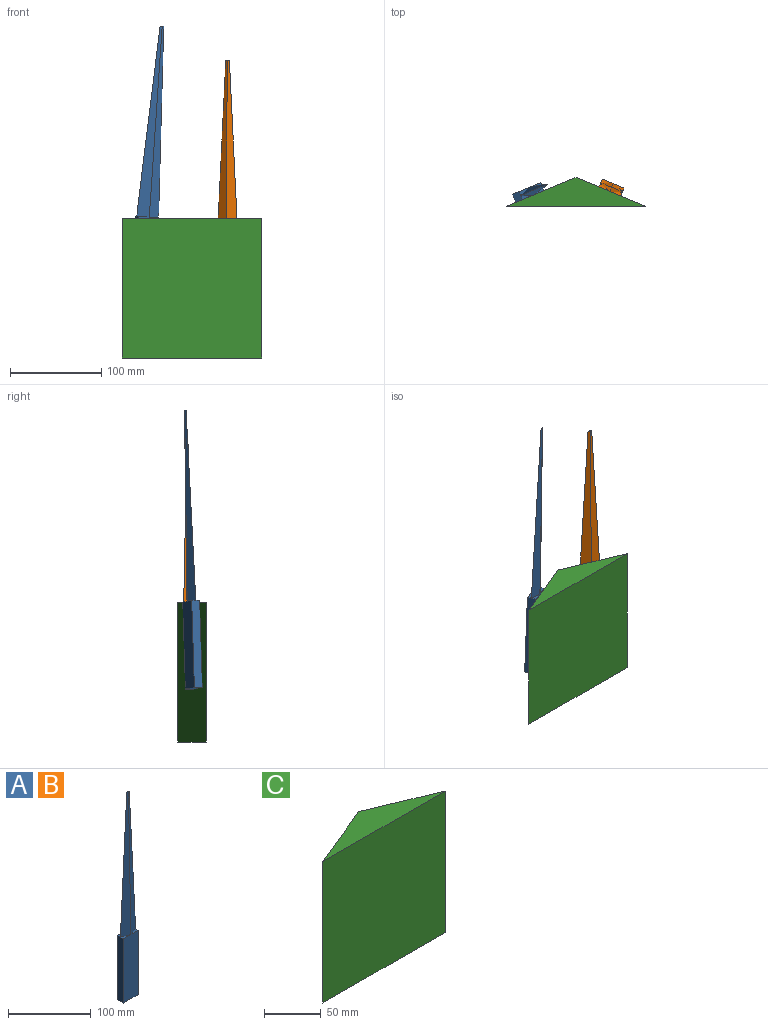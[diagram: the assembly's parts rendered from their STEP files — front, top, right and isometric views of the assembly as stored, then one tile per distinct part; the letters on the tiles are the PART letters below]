
ASSEMBLY  parts=3 mates=2
PART A: 14 faces, bbox 25.4x9.5x304.8 mm
  f0: plane 101.6x9.53mm, normal (1,0,0), area 908.5mm2, adj f1,f3,f5,f6,f7,f10,f11
  f1: plane 101.6x25.4mm, normal (0,1,0), area 2423.7mm2, adj f0,f2,f5,f10,f11,f12,f13
  f2: plane 101.6x9.53mm, normal (-1,0,0), area 908.5mm2, adj f1,f3,f5,f8,f9,f12,f13
  f3: plane 101.6x25.4mm, normal (0,-1,0), area 2423.7mm2, adj f0,f2,f5,f6,f7,f8,f9
  f4: plane 4.27x1.6mm, normal (0,0,1), area 3.4mm2, adj f7,f9,f10,f13
  f5: plane 25.4x9.53mm, normal (0,0,-1), area 241.9mm2, adj f0,f1,f2,f3
  f6: plane 12.37x4.64mm, normal (0,0.02,1), area 28.7mm2, adj f0,f3,f7
  f7: plane 209.55x12.7mm, normal (0.35,-0.94,0.02), area 1694.3mm2, adj f0,f3,f4,f6,f9,f10
  f8: plane 12.37x4.64mm, normal (0,0.02,1), area 28.7mm2, adj f2,f3,f9
  f9: plane 209.55x12.7mm, normal (-0.35,-0.94,0.02), area 1694.3mm2, adj f2,f3,f4,f7,f8,f13
  f10: plane 209.55x12.7mm, normal (0.35,0.94,0.02), area 1694.3mm2, adj f0,f1,f4,f7,f11,f13
  f11: plane 12.37x4.64mm, normal (0,-0.02,1), area 28.7mm2, adj f0,f1,f10
  f12: plane 12.37x4.64mm, normal (0,-0.02,1), area 28.7mm2, adj f1,f2,f13
  f13: plane 209.55x12.7mm, normal (-0.35,0.94,0.02), area 1694.3mm2, adj f1,f2,f4,f9,f10,f12
PART B: same geometry as A
PART C: 5 faces, bbox 152.4x31.6x152.4 mm
  f0: plane 152.4x76.2mm, normal (-0.38,0.92,0), area 12569.7mm2, adj f1,f2,f3,f4
  f1: plane 152.4x152.4mm, normal (0,-1,0), area 23225.8mm2, adj f0,f2,f3,f4
  f2: plane 152.4x76.2mm, normal (0.38,0.92,0), area 12569.7mm2, adj f0,f1,f3,f4
  f3: plane 152.4x31.56mm, normal (0,0,1), area 2405.1mm2, adj f0,f1,f2
  f4: plane 152.4x31.56mm, normal (0,0,-1), area 2405.1mm2, adj f0,f1,f2
PLACE A rot(axis=(-0.04,0.2,0.98),23deg) t=(-26.4,-14.05,126.68)mm
PLACE B rot(axis=(0,0,-1),22.5deg) t=(60.62,-10.24,88.34)mm
PLACE C t=(21.71,-30.84,-33.53)mm fixed
MATE planar A.f3 <-> C.f0  axis (0.38,-0.92,0) through (-28.6,-20.12,72.97)mm
MATE planar C.f2 <-> B.f3  axis (0.38,0.92,0) through (59.81,-15.06,42.67)mm
